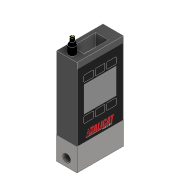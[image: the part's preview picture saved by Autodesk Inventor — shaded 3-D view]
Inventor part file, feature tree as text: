
AUTODESK INVENTOR PART (.ipt)
format: ipt  version: 2022 (Build 260153000, 153)  size: 217,600 bytes
history: native  units: mm
features: sketch x11, extrude x8, other x4, split x1, plane x1, loft x1, boolean_combine x1
ambient origin geometry x8: Origin, YZ Plane, XZ Plane, XY Plane, X Axis, Y Axis, Z Axis, Center Point
bodies: Solid1 (feature_tree), Solid4 (feature_tree), Solid5 (feature_tree), Solid2 (feature_tree), Solid3 (feature_tree)
feature tree (27):
  extrude  "Extrusion1"  Depth=61.0mm
  split  "Split1"
  extrude  "Extrusion2"  Depth=30.0mm
  extrude  "Extrusion3"  Depth=10.0mm
  other  "Decal2"
  extrude  "Extrusion4"  Depth=4.0mm
  extrude  "Extrusion5"  Depth=10.0mm
  extrude  "Extrusion6"  Depth=8.0mm
  extrude  "Extrusion7"  Depth=4.0mm
  plane  "Work Plane4"
  extrude  "Extrusion8"  Depth=16.65mm
  loft  "Loft1"
  boolean_combine  "Combine1"
  sketch  "Sketch18"  dims[d45=8.0mm d46=1.0mm d47=0.0mm d48=6.0mm d49=7.0mm d50=0.0mm d51=9.0mm d52=10.0mm d53=0.0mm d54=4.0mm d55=5.0mm d56=5.0mm d57=0.0mm d58=0.0mm d59=90.0deg d60=0.0mm d61=90.0deg]
  sketch  "Sketch1"  dims[d0=27.0mm d1=61.0mm]
  sketch  "Sketch2"  dims[d2=125.0mm d3=0.0mm d4=30.0mm]
  sketch  "Sketch3"  dims[d5=10.0mm d6=10.0mm]
  sketch  "Sketch4"  dims[d7=4.0mm d8=4.0mm]
  sketch  "Sketch12"  dims[d9=10.0mm d10=0.0mm d11=10.0mm]
  other  "Image2"
  sketch  "Sketch13"  dims[d12=10.0mm d13=0.0mm d14=8.0mm]
  sketch  "Sketch14"  dims[d15=8.0mm d16=4.0mm]
  sketch  "Sketch15"  dims[d39=30.5mm d40=16.65mm]
  sketch  "Sketch16"  dims[d41=31.8mm d42=16.2mm d43=0.0mm]
  sketch  "Sketch17"  dims[d44=7.3mm]
  other  "Edges1"
  other  "Edges2"
